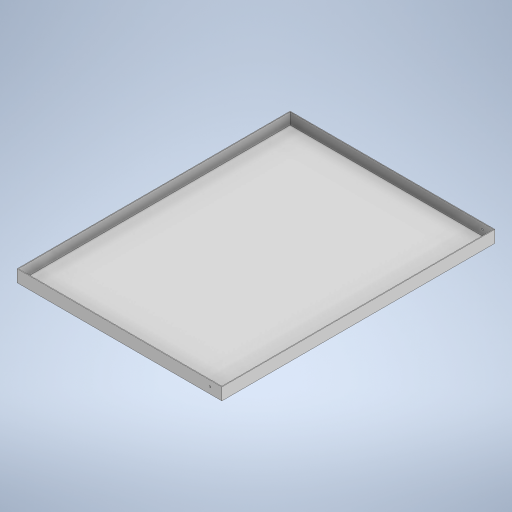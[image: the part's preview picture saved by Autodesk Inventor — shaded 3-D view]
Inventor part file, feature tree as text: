
AUTODESK INVENTOR PART (.ipt)
format: ipt  version: 2024 (Build 280153000, 153)  size: 251,392 bytes
history: native  units: mm
features: extrude x3, sketch x3, other x1
ambient origin geometry x8: Origin, YZ Plane, XZ Plane, XY Plane, X Axis, Y Axis, Z Axis, Center Point
bodies: Body1 (feature_tree)
feature tree (7):
  other  "Sólido1"
  extrude  "Extrusión1"  Depth=1200.0mm
  extrude  "Extrusión2"  Depth=3.0mm
  extrude  "Extrusión3"  Depth=3.0mm
  sketch  "Boceto1"  dims[d0=900.0mm d1=1200.0mm]
  sketch  "Boceto2"  dims[d2=3.0mm d3=0.0mm d4=3.0mm]
  sketch  "Boceto3"  dims[d5=50.0mm d6=0.0mm d7=8.0mm d8=25.0mm d9=3.0mm d10=55.0mm d11=1243.5mm d12=0.0mm]
